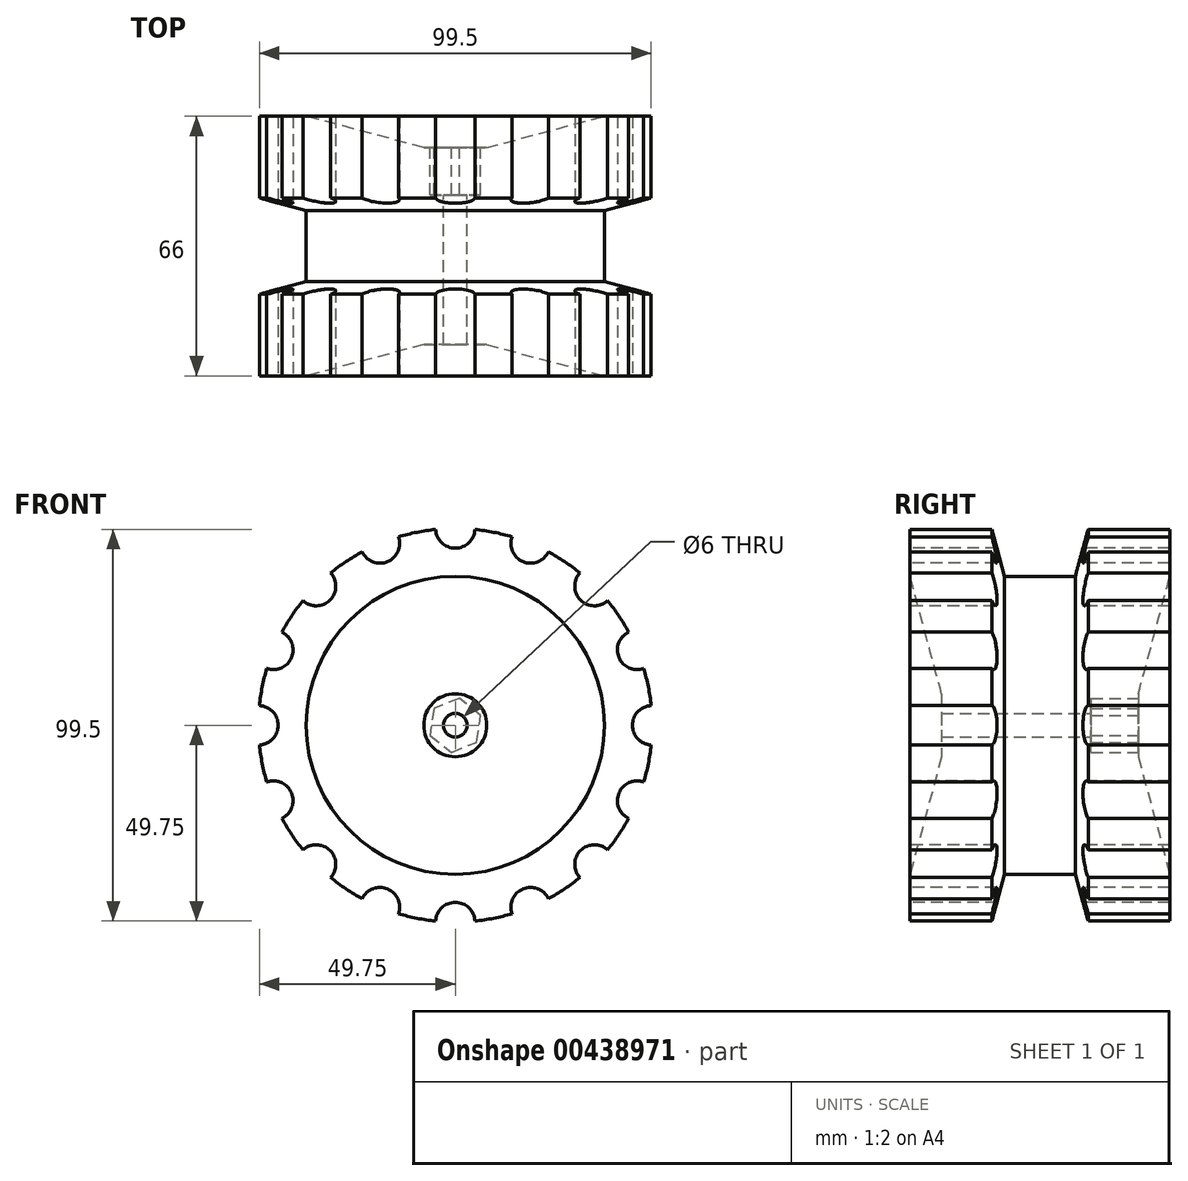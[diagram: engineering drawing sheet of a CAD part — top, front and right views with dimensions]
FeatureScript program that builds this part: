
annotation { "Feature Type Name" : "Feature", "Feature Type Description" : "" }
export const myFeature = defineFeature(function(context is Context, id is Id, definition is map)
    precondition{}
    {
        {
            var Q0;
            Q0=qCreatedBy(makeId("Front.planeOp"),FACE);
            var sketch = newSketch(context, id + "F0", { "sketchPlane" : qUnion([Q0])});
            skCircle(sketch, "E0", {"center": v(0, 0) * mm, "radius": 50 * mm});
            skSolve(sketch);
        }
        {
            var Q0;
            Q0=makeQuery(id+"F0.imprint","IMPRINT",FACE,{"disambiguationData":[TD([[makeQuery(id+"F0.imprint","IMPRINT",EDGE,{"derivedFrom":sQuery(id+"F0.wireOp",EDGE,"E0")}),1.0]])]});
            extrude(context, id + "F1", {"entities" : qUnion([Q0]), "depth" : 66 * mm});
        }
        {
            var Q0;
            Q0=makeQuery(id+"F1.opExtrude","CAP_FACE",FACE,{"disambiguationData":[OSD([sQuery(id+"F0.wireOp",EDGE,"E0")])],"isStart":false});
            var sketch = newSketch(context, id + "F2", { "sketchPlane" : qUnion([Q0])});
            skPoint(sketch, "E1.center", {"position": v(0, 0) * mm});
            skCircle(sketch, "E2", {"center": v(0, 50) * mm, "radius": 5 * mm});
            skCircle(sketch, "E3", {"center": v(0, -50) * mm, "radius": 5 * mm});
            skCircle(sketch, "E4", {"center": v(50, 0) * mm, "radius": 5 * mm});
            skCircle(sketch, "E5", {"center": v(-50, 0) * mm, "radius": 5 * mm});
            skCircle(sketch, "E6", {"center": v(35.36, 35.36) * mm, "radius": 5 * mm});
            skLineSegment(sketch, "E7", {"start": v(-53.03, 53.03) * mm, "end": v(53.03, -53.03) * mm, "construction": true});
            skLineSegment(sketch, "E8", {"start": v(-53.03, -53.03) * mm, "end": v(53.03, 53.03) * mm, "construction": true});
            skCircle(sketch, "E9", {"center": v(35.36, -35.36) * mm, "radius": 5 * mm});
            skCircle(sketch, "E10", {"center": v(19.13, -46.2) * mm, "radius": 5 * mm});
            skCircle(sketch, "E11", {"center": v(-35.36, -35.36) * mm, "radius": 5 * mm});
            skCircle(sketch, "E12", {"center": v(-35.36, 35.36) * mm, "radius": 5 * mm});
            skLineSegment(sketch, "E13", {"start": v(28.7, 69.3) * mm, "end": v(-28.7, -69.3) * mm, "construction": true});
            skLineSegment(sketch, "E14", {"start": v(69.3, 28.7) * mm, "end": v(-69.3, -28.7) * mm, "construction": true});
            skLineSegment(sketch, "E15", {"start": v(69.3, -28.7) * mm, "end": v(-69.3, 28.7) * mm, "construction": true});
            skLineSegment(sketch, "E16", {"start": v(28.7, -69.3) * mm, "end": v(-28.7, 69.3) * mm, "construction": true});
            skCircle(sketch, "E17", {"center": v(0, 0) * mm, "radius": 75 * mm, "construction": true});
            skCircle(sketch, "E18", {"center": v(46.2, -19.13) * mm, "radius": 5 * mm});
            skCircle(sketch, "E19", {"center": v(46.2, 19.13) * mm, "radius": 5 * mm});
            skCircle(sketch, "E20", {"center": v(19.13, 46.2) * mm, "radius": 5 * mm});
            skCircle(sketch, "E21", {"center": v(-19.13, 46.2) * mm, "radius": 5 * mm});
            skCircle(sketch, "E22", {"center": v(-46.2, 19.13) * mm, "radius": 5 * mm});
            skCircle(sketch, "E23", {"center": v(-46.2, -19.13) * mm, "radius": 5 * mm});
            skCircle(sketch, "E24", {"center": v(-19.13, -46.2) * mm, "radius": 5 * mm});
            skSolve(sketch);
        }
        {
            var Q0;
            {var subQ0=sQuery(id+"F2.wireOp",EDGE,"E12");var subQ1=makeQuery(id+"F1.opExtrude","CAP_EDGE",EDGE,{"disambiguationData":[OSD([sQuery(id+"F0.wireOp",EDGE,"E0")])],"isStart":false});var subQ2=makeQuery(id+"F2.imprint","INTERSECT",VERTEX,{"disambiguationData":[OD(0.0)],"derivedFrom":[subQ1,subQ0]});Q0=makeQuery(id+"F2.imprint","IMPRINT",FACE,{"disambiguationData":[TD([[makeQuery(id+"F2.imprint","IMPRINT",EDGE,{"disambiguationData":[TD([[subQ2,-1.0]])],"derivedFrom":subQ0}),1.0]])]});}
            var Q1;
            {var subQ0=sQuery(id+"F2.wireOp",EDGE,"E21");var subQ1=makeQuery(id+"F1.opExtrude","CAP_EDGE",EDGE,{"disambiguationData":[OSD([sQuery(id+"F0.wireOp",EDGE,"E0")])],"isStart":false});var subQ2=makeQuery(id+"F2.imprint","INTERSECT",VERTEX,{"disambiguationData":[OD(0.0)],"derivedFrom":[subQ1,subQ0]});Q1=makeQuery(id+"F2.imprint","IMPRINT",FACE,{"disambiguationData":[TD([[makeQuery(id+"F2.imprint","IMPRINT",EDGE,{"disambiguationData":[TD([[subQ2,-1.0]])],"derivedFrom":subQ0}),1.0]])]});}
            var Q2;
            {var subQ0=sQuery(id+"F2.wireOp",EDGE,"E2");var subQ1=makeQuery(id+"F1.opExtrude","CAP_EDGE",EDGE,{"disambiguationData":[OSD([sQuery(id+"F0.wireOp",EDGE,"E0")])],"isStart":false});var subQ2=makeQuery(id+"F2.imprint","INTERSECT",VERTEX,{"disambiguationData":[OD(0.0)],"derivedFrom":[subQ1,subQ0]});Q2=makeQuery(id+"F2.imprint","IMPRINT",FACE,{"disambiguationData":[TD([[makeQuery(id+"F2.imprint","IMPRINT",EDGE,{"disambiguationData":[TD([[subQ2,-1.0]])],"derivedFrom":subQ0}),1.0]])]});}
            var Q3;
            {var subQ0=sQuery(id+"F2.wireOp",EDGE,"E20");var subQ1=makeQuery(id+"F1.opExtrude","CAP_EDGE",EDGE,{"disambiguationData":[OSD([sQuery(id+"F0.wireOp",EDGE,"E0")])],"isStart":false});var subQ2=makeQuery(id+"F2.imprint","INTERSECT",VERTEX,{"disambiguationData":[OD(0.0)],"derivedFrom":[subQ1,subQ0]});Q3=makeQuery(id+"F2.imprint","IMPRINT",FACE,{"disambiguationData":[TD([[makeQuery(id+"F2.imprint","IMPRINT",EDGE,{"disambiguationData":[TD([[subQ2,-1.0]])],"derivedFrom":subQ0}),1.0]])]});}
            var Q4;
            {var subQ0=sQuery(id+"F2.wireOp",EDGE,"E6");var subQ1=makeQuery(id+"F1.opExtrude","CAP_EDGE",EDGE,{"disambiguationData":[OSD([sQuery(id+"F0.wireOp",EDGE,"E0")])],"isStart":false});var subQ2=makeQuery(id+"F2.imprint","INTERSECT",VERTEX,{"disambiguationData":[OD(0.0)],"derivedFrom":[subQ1,subQ0]});Q4=makeQuery(id+"F2.imprint","IMPRINT",FACE,{"disambiguationData":[TD([[makeQuery(id+"F2.imprint","IMPRINT",EDGE,{"disambiguationData":[TD([[subQ2,-1.0]])],"derivedFrom":subQ0}),1.0]])]});}
            var Q5;
            {var subQ0=sQuery(id+"F2.wireOp",EDGE,"E19");var subQ1=makeQuery(id+"F1.opExtrude","CAP_EDGE",EDGE,{"disambiguationData":[OSD([sQuery(id+"F0.wireOp",EDGE,"E0")])],"isStart":false});var subQ2=makeQuery(id+"F2.imprint","INTERSECT",VERTEX,{"disambiguationData":[OD(0.0)],"derivedFrom":[subQ1,subQ0]});Q5=makeQuery(id+"F2.imprint","IMPRINT",FACE,{"disambiguationData":[TD([[makeQuery(id+"F2.imprint","IMPRINT",EDGE,{"disambiguationData":[TD([[subQ2,-1.0]])],"derivedFrom":subQ0}),1.0]])]});}
            var Q6;
            {var subQ0=sQuery(id+"F2.wireOp",EDGE,"E4");var subQ1=makeQuery(id+"F1.opExtrude","CAP_EDGE",EDGE,{"disambiguationData":[OSD([sQuery(id+"F0.wireOp",EDGE,"E0")])],"isStart":false});var subQ2=makeQuery(id+"F2.imprint","INTERSECT",VERTEX,{"disambiguationData":[OD(0.0)],"derivedFrom":[subQ1,subQ0]});Q6=makeQuery(id+"F2.imprint","IMPRINT",FACE,{"disambiguationData":[TD([[makeQuery(id+"F2.imprint","IMPRINT",EDGE,{"disambiguationData":[TD([[subQ2,1.0]])],"derivedFrom":subQ0}),1.0]])]});}
            var Q7;
            {var subQ0=sQuery(id+"F2.wireOp",EDGE,"E18");var subQ1=makeQuery(id+"F1.opExtrude","CAP_EDGE",EDGE,{"disambiguationData":[OSD([sQuery(id+"F0.wireOp",EDGE,"E0")])],"isStart":false});var subQ2=makeQuery(id+"F2.imprint","INTERSECT",VERTEX,{"disambiguationData":[OD(0.0)],"derivedFrom":[subQ1,subQ0]});Q7=makeQuery(id+"F2.imprint","IMPRINT",FACE,{"disambiguationData":[TD([[makeQuery(id+"F2.imprint","IMPRINT",EDGE,{"disambiguationData":[TD([[subQ2,1.0]])],"derivedFrom":subQ0}),1.0]])]});}
            var Q8;
            {var subQ0=sQuery(id+"F2.wireOp",EDGE,"E9");var subQ1=makeQuery(id+"F1.opExtrude","CAP_EDGE",EDGE,{"disambiguationData":[OSD([sQuery(id+"F0.wireOp",EDGE,"E0")])],"isStart":false});var subQ2=makeQuery(id+"F2.imprint","INTERSECT",VERTEX,{"disambiguationData":[OD(0.0)],"derivedFrom":[subQ1,subQ0]});Q8=makeQuery(id+"F2.imprint","IMPRINT",FACE,{"disambiguationData":[TD([[makeQuery(id+"F2.imprint","IMPRINT",EDGE,{"disambiguationData":[TD([[subQ2,1.0]])],"derivedFrom":subQ0}),1.0]])]});}
            var Q9;
            {var subQ0=sQuery(id+"F2.wireOp",EDGE,"E10");var subQ1=makeQuery(id+"F1.opExtrude","CAP_EDGE",EDGE,{"disambiguationData":[OSD([sQuery(id+"F0.wireOp",EDGE,"E0")])],"isStart":false});var subQ2=makeQuery(id+"F2.imprint","INTERSECT",VERTEX,{"disambiguationData":[OD(0.0)],"derivedFrom":[subQ1,subQ0]});Q9=makeQuery(id+"F2.imprint","IMPRINT",FACE,{"disambiguationData":[TD([[makeQuery(id+"F2.imprint","IMPRINT",EDGE,{"disambiguationData":[TD([[subQ2,1.0]])],"derivedFrom":subQ0}),1.0]])]});}
            var Q10;
            {var subQ0=sQuery(id+"F2.wireOp",EDGE,"E3");var subQ1=makeQuery(id+"F1.opExtrude","CAP_EDGE",EDGE,{"disambiguationData":[OSD([sQuery(id+"F0.wireOp",EDGE,"E0")])],"isStart":false});var subQ2=makeQuery(id+"F2.imprint","INTERSECT",VERTEX,{"disambiguationData":[OD(0.0)],"derivedFrom":[subQ1,subQ0]});Q10=makeQuery(id+"F2.imprint","IMPRINT",FACE,{"disambiguationData":[TD([[makeQuery(id+"F2.imprint","IMPRINT",EDGE,{"disambiguationData":[TD([[subQ2,1.0]])],"derivedFrom":subQ0}),1.0]])]});}
            var Q11;
            {var subQ0=sQuery(id+"F2.wireOp",EDGE,"E24");var subQ1=makeQuery(id+"F1.opExtrude","CAP_EDGE",EDGE,{"disambiguationData":[OSD([sQuery(id+"F0.wireOp",EDGE,"E0")])],"isStart":false});var subQ2=makeQuery(id+"F2.imprint","INTERSECT",VERTEX,{"disambiguationData":[OD(0.0)],"derivedFrom":[subQ1,subQ0]});Q11=makeQuery(id+"F2.imprint","IMPRINT",FACE,{"disambiguationData":[TD([[makeQuery(id+"F2.imprint","IMPRINT",EDGE,{"disambiguationData":[TD([[subQ2,1.0]])],"derivedFrom":subQ0}),1.0]])]});}
            var Q12;
            {var subQ0=sQuery(id+"F2.wireOp",EDGE,"E11");var subQ1=makeQuery(id+"F1.opExtrude","CAP_EDGE",EDGE,{"disambiguationData":[OSD([sQuery(id+"F0.wireOp",EDGE,"E0")])],"isStart":false});var subQ2=makeQuery(id+"F2.imprint","INTERSECT",VERTEX,{"disambiguationData":[OD(0.0)],"derivedFrom":[subQ1,subQ0]});Q12=makeQuery(id+"F2.imprint","IMPRINT",FACE,{"disambiguationData":[TD([[makeQuery(id+"F2.imprint","IMPRINT",EDGE,{"disambiguationData":[TD([[subQ2,1.0]])],"derivedFrom":subQ0}),1.0]])]});}
            var Q13;
            {var subQ0=sQuery(id+"F2.wireOp",EDGE,"E23");var subQ1=makeQuery(id+"F1.opExtrude","CAP_EDGE",EDGE,{"disambiguationData":[OSD([sQuery(id+"F0.wireOp",EDGE,"E0")])],"isStart":false});var subQ2=makeQuery(id+"F2.imprint","INTERSECT",VERTEX,{"disambiguationData":[OD(0.0)],"derivedFrom":[subQ1,subQ0]});Q13=makeQuery(id+"F2.imprint","IMPRINT",FACE,{"disambiguationData":[TD([[makeQuery(id+"F2.imprint","IMPRINT",EDGE,{"disambiguationData":[TD([[subQ2,1.0]])],"derivedFrom":subQ0}),1.0]])]});}
            var Q14;
            {var subQ0=sQuery(id+"F2.wireOp",EDGE,"E5");var subQ1=makeQuery(id+"F1.opExtrude","CAP_EDGE",EDGE,{"disambiguationData":[OSD([sQuery(id+"F0.wireOp",EDGE,"E0")])],"isStart":false});var subQ2=makeQuery(id+"F2.imprint","INTERSECT",VERTEX,{"disambiguationData":[OD(0.0)],"derivedFrom":[subQ1,subQ0]});Q14=makeQuery(id+"F2.imprint","IMPRINT",FACE,{"disambiguationData":[TD([[makeQuery(id+"F2.imprint","IMPRINT",EDGE,{"disambiguationData":[TD([[subQ2,-1.0]])],"derivedFrom":subQ0}),1.0]])]});}
            var Q15;
            {var subQ0=sQuery(id+"F2.wireOp",EDGE,"E22");var subQ1=makeQuery(id+"F1.opExtrude","CAP_EDGE",EDGE,{"disambiguationData":[OSD([sQuery(id+"F0.wireOp",EDGE,"E0")])],"isStart":false});var subQ2=makeQuery(id+"F2.imprint","INTERSECT",VERTEX,{"disambiguationData":[OD(0.0)],"derivedFrom":[subQ1,subQ0]});Q15=makeQuery(id+"F2.imprint","IMPRINT",FACE,{"disambiguationData":[TD([[makeQuery(id+"F2.imprint","IMPRINT",EDGE,{"disambiguationData":[TD([[subQ2,-1.0]])],"derivedFrom":subQ0}),1.0]])]});}
            extrude(context, id + "F3", {"entities" : qUnion([Q0, Q1, Q2, Q3, Q4, Q5, Q6, Q7, Q8, Q9, Q10, Q11, Q12, Q13, Q14, Q15]), "operationType" : NewBodyOperationType.REMOVE, "oppositeDirection" : true, "depth" : 66 * mm});
        }
        {
            var Q0;
            Q0=qCreatedBy(makeId("Right.planeOp"),FACE);
            var sketch = newSketch(context, id + "F4", { "sketchPlane" : qUnion([Q0])});
            skLineSegment(sketch, "E25", {"start": v(-20, 52.86) * mm, "end": v(-24.02, 37.86) * mm});
            skLineSegment(sketch, "E26", {"start": v(-24.02, 37.86) * mm, "end": v(-41.98, 37.86) * mm});
            skLineSegment(sketch, "E27", {"start": v(-41.98, 37.86) * mm, "end": v(-46, 52.86) * mm});
            skLineSegment(sketch, "E28", {"start": v(0, 37.86) * mm, "end": v(-66, 37.86) * mm, "construction": true});
            skPoint(sketch, "E29", {"position": v(-66, 37.86) * mm});
            skLineSegment(sketch, "E30", {"start": v(-66, 37.86) * mm, "end": v(-58, 8) * mm});
            skLineSegment(sketch, "E31", {"start": v(-58, 8) * mm, "end": v(-58, 0) * mm});
            skLineSegment(sketch, "E32", {"start": v(-66, 37.86) * mm, "end": v(-66, 0) * mm});
            skLineSegment(sketch, "E33", {"start": v(-66, 0) * mm, "end": v(-58, 0) * mm});
            skLineSegment(sketch, "E34", {"start": v(-66, 0) * mm, "end": v(42.48, 0) * mm, "construction": true});
            skLineSegment(sketch, "E35", {"start": v(0, 37.86) * mm, "end": v(-8, 8) * mm});
            skLineSegment(sketch, "E36", {"start": v(0, 50) * mm, "end": v(0, -55.59) * mm, "construction": true});
            skLineSegment(sketch, "E37", {"start": v(-66, 0) * mm, "end": v(-66, 69.44) * mm, "construction": true});
            skLineSegment(sketch, "E38", {"start": v(-8, 8) * mm, "end": v(-8, 0) * mm});
            skLineSegment(sketch, "E39", {"start": v(-8, 0) * mm, "end": v(0, 0) * mm});
            skLineSegment(sketch, "E40", {"start": v(0, 0) * mm, "end": v(0, 37.86) * mm});
            skLineSegment(sketch, "E41", {"start": v(0, 50) * mm, "end": v(-78.1, 50) * mm});
            skLineSegment(sketch, "E42", {"start": v(-20, 52.86) * mm, "end": v(-46, 52.86) * mm});
            skSolve(sketch);
        }
        {
            var Q0;
            Q0 = qSketchRegion(id + "F4", true);
            var Q1;
            Q1=sQuery(id+"F4.wireOp",EDGE,"E34");
            revolve(context, id + "F5", {"operationType" : NewBodyOperationType.REMOVE, "entities" : qUnion([Q0]), "axis" : qUnion([Q1]), "revolveType" : RevolveType.FULL, "oppositeDirection" : true});
        }
        {
            var Q0;
            Q0=makeQuery(id+"F5.boolean.opBoolean","COPY",FACE,{"derivedFrom":makeQuery(id+"F5.opRevolve","SWEPT_FACE",FACE,{"disambiguationData":[OSD([sQuery(id+"F4.wireOp",EDGE,"E38")])]})});
            var sketch = newSketch(context, id + "F6", { "sketchPlane" : qUnion([Q0])});
            skCircle(sketch, "E43.cCircle", {"center": v(0, 0) * mm, "radius": 6 * mm, "construction": true});
            skLineSegment(sketch, "E43.0", {"start": v(6.44, -2.55) * mm, "end": v(1.02, -6.85) * mm});
            skLineSegment(sketch, "E43.1", {"start": v(1.02, -6.85) * mm, "end": v(-5.43, -4.3) * mm});
            skLineSegment(sketch, "E43.2", {"start": v(-5.43, -4.3) * mm, "end": v(-6.44, 2.55) * mm});
            skLineSegment(sketch, "E43.3", {"start": v(-6.44, 2.55) * mm, "end": v(-1.02, 6.85) * mm});
            skLineSegment(sketch, "E43.4", {"start": v(-1.02, 6.85) * mm, "end": v(5.43, 4.3) * mm});
            skLineSegment(sketch, "E43.5", {"start": v(5.43, 4.3) * mm, "end": v(6.44, -2.55) * mm});
            skPoint(sketch, "E43.0.midPoint", {"position": v(3.73, -4.7) * mm});
            skCircle(sketch, "E44", {"center": v(0, 0) * mm, "radius": 3 * mm});
            skSolve(sketch);
        }
        {
            var Q0;
            Q0=makeQuery(id+"F6.imprint","IMPRINT",FACE,{"disambiguationData":[TD([[makeQuery(id+"F6.imprint","IMPRINT",EDGE,{"derivedFrom":sQuery(id+"F6.wireOp",EDGE,"E43.0")}),-1.0]])]});
            extrude(context, id + "F7", {"entities" : qUnion([Q0]), "operationType" : NewBodyOperationType.REMOVE, "oppositeDirection" : true, "depth" : 12 * mm});
        }
        {
            var Q0;
            Q0=makeQuery(id+"F7.boolean.opBoolean","SPLIT",FACE,{"disambiguationData":[TD([makeQuery(id+"F7.opExtrude","SWEPT_FACE",FACE,{"disambiguationData":[OSD([sQuery(id+"F6.wireOp",EDGE,"E44")])]})])],"derivedFrom":makeQuery(id+"F5.boolean.opBoolean","COPY",FACE,{"derivedFrom":makeQuery(id+"F5.opRevolve","SWEPT_FACE",FACE,{"disambiguationData":[OSD([sQuery(id+"F4.wireOp",EDGE,"E38")])]})})});
            extrude(context, id + "F8", {"entities" : qUnion([Q0]), "operationType" : NewBodyOperationType.REMOVE, "oppositeDirection" : true, "depth" : 50 * mm});
        }
    });
